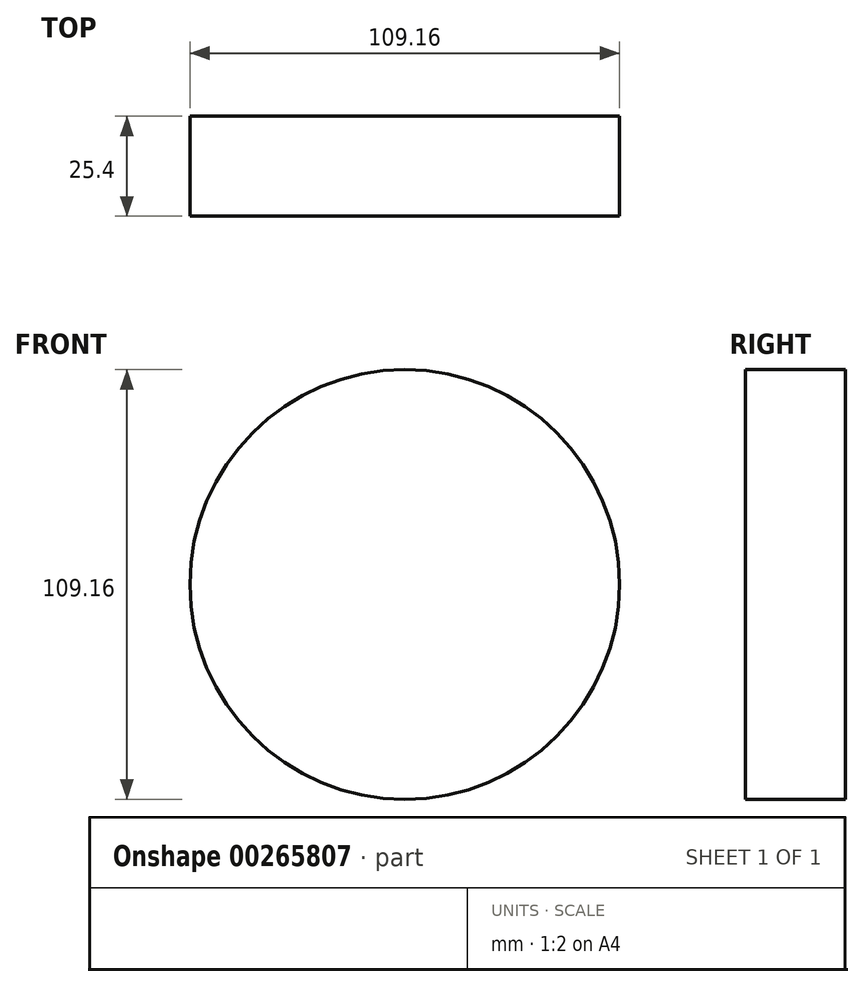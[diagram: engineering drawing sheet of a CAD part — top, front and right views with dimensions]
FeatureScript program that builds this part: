
annotation { "Feature Type Name" : "Feature", "Feature Type Description" : "" }
export const myFeature = defineFeature(function(context is Context, id is Id, definition is map)
    precondition{}
    {
        {
            var Q0;
            Q0=qCreatedBy(makeId("Front.planeOp"),FACE);
            var sketch = newSketch(context, id + "F0", { "sketchPlane" : qUnion([Q0])});
            skCircle(sketch, "E0", {"center": v(0, 0) * mm, "radius": 54.58 * mm});
            skSolve(sketch);
        }
        {
            var Q0;
            Q0=makeQuery(id+"F0.imprint","IMPRINT",FACE,{"disambiguationData":[TD([[makeQuery(id+"F0.imprint","IMPRINT",EDGE,{"derivedFrom":sQuery(id+"F0.wireOp",EDGE,"E0")}),1.0]])]});
            extrude(context, id + "F1", {"entities" : qUnion([Q0]), "depth" : 25.4 * mm});
        }
    });
